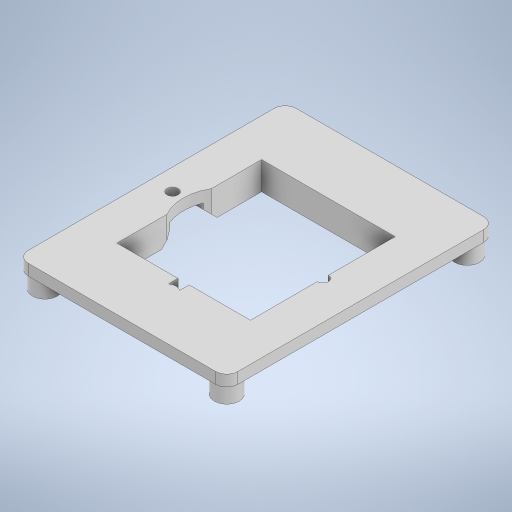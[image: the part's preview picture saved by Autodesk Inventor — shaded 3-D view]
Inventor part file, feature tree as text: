
AUTODESK INVENTOR PART (.ipt)
format: ipt  version: 2024.2 (Build 282272000, 272)  size: 370,688 bytes
history: native  units: mm
features: extrude x9, sketch x9, fillet x2, chamfer x1
ambient origin geometry x8: Origin, YZ Plane, XZ Plane, XY Plane, X Axis, Y Axis, Z Axis, Center Point
bodies: Solid1 (feature_tree)
feature tree (21):
  extrude  "Extrusion1"  Depth=38.5mm
  extrude  "Extrusion2"  Depth=26.0mm
  extrude  "Extrusion3"  Depth=3.0mm
  extrude  "Extrusion4"  Depth=4.0mm
  fillet  "Fillet1"  Radius=4.0mm
  extrude  "Extrusion6"  Depth=48.2mm
  extrude  "Extrusion7"  Depth=4.85mm
  chamfer  "Chamfer1"  Distance=2.0mm
  extrude  "Extrusion8"  Depth=2.35mm
  extrude  "Extrusion9"  Depth=2.0mm
  extrude  "Extrusion10"  Depth=2.0mm
  fillet  "Fillet2"  Radius=2.35mm
  sketch  "Sketch1"  dims[d0=28.0mm d1=38.5mm]
  sketch  "Sketch2"  dims[d2=24.0mm d3=26.0mm]
  sketch  "Sketch3"  dims[d6=3.0mm d7=0.0mm d8=4.0mm]
  sketch  "Sketch4"  dims[d9=4.0mm d10=4.0mm d11=4.0mm]
  sketch  "Sketch5"  dims[d12=3.0mm d13=0.0mm d14=48.2mm]
  sketch  "Sketch6"  dims[d15=37.7mm d16=4.85mm]
  sketch  "Sketch7"  dims[d17=4.85mm d18=2.0mm d19=0.0mm]
  sketch  "Sketch8"  dims[d20=4.5mm d21=2.35mm]
  sketch  "Sketch9"  dims[d22=2.35mm d23=4.5mm d24=2.35mm d25=2.35mm d26=4.5mm d27=2.35mm d28=4.5mm d29=2.35mm d30=2.35mm d31=2.35mm d32=3.0mm d33=0.0mm d34=2.0mm d43=2.0mm d44=6.25mm d45=2.0mm d46=2.0mm d47=13.0mm d50=13.0mm d51=0.0mm d52=0.0mm d53=6.0mm d54=21.1mm d55=10.0mm d56=0.0mm d57=2.0mm d58=2.0mm d59=45.0deg d63=8.0mm d64=20.1mm d65=8.0mm d66=10.0mm d67=0.0mm d68=3.5mm d69=3.125mm d70=18.85mm d71=0.0mm d72=0.0mm d73=27.0mm d75=3.0mm d76=2.0mm d77=1.0mm d78=0.0mm d79=0.0mm d80=2.0mm]
